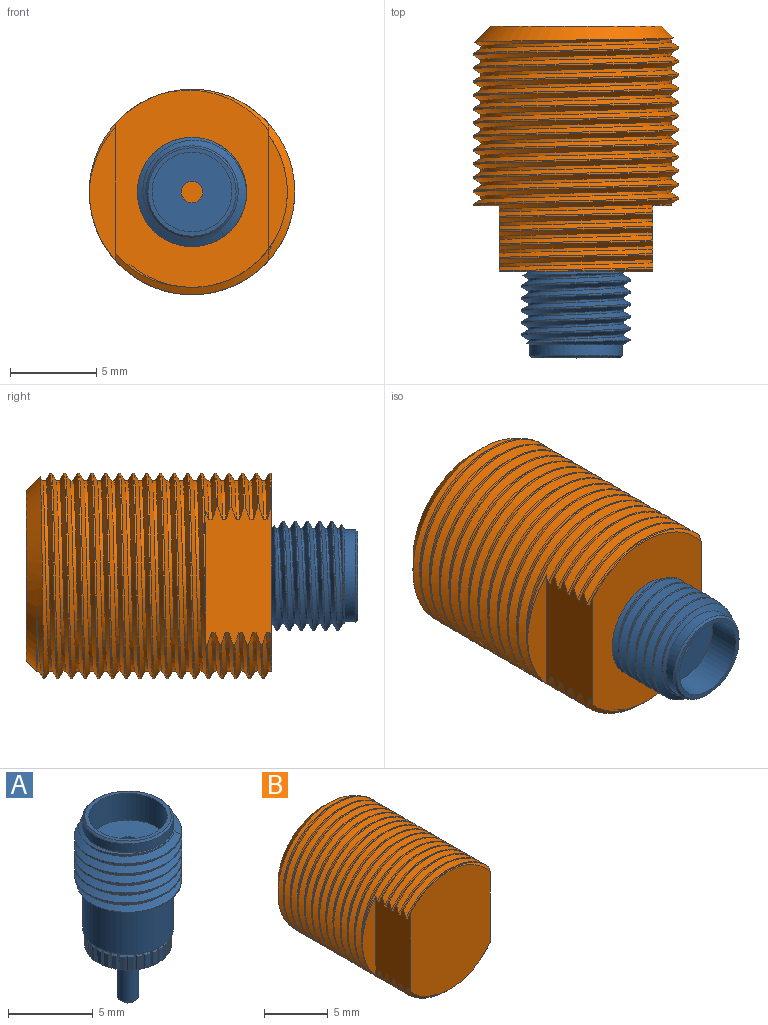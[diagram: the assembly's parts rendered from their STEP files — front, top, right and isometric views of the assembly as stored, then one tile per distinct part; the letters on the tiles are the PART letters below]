
ASSEMBLY  parts=2 mates=1
PART A: 177 faces, bbox 7.3x6.4x13.2 mm
  f0: cone r=0.38mm half-angle=45deg, axis (0,0,1), area 1.1mm2, adj f1,f176
  f1: cylinder r=0.64mm len=4.85mm, axis (0,0,1), area 19.4mm2, adj f0,f15
  f2: cylinder r=0.62mm len=6.2mm, axis (0,0,1), area 24.3mm2, adj f109,f175
  f3: cylinder r=2.74mm len=5.49mm, axis (0,0,-1), area 13.6mm2, adj f11,f12,f172,f173
  f4: cone r=2.67mm half-angle=45deg, axis (0,0,-1), area 2.8mm2, adj f6,f108
  f5: cylinder r=2.31mm len=4.63mm, axis (0,0,-1), area 28.1mm2, adj f108,f109
  f6: cylinder r=2.67mm len=5.35mm, axis (0,0,-1), area 10.8mm2, adj f4,f11
  f7: cylinder r=2.67mm len=5.35mm, axis (0,0,-1), area 52.1mm2, adj f12,f16
  f8: cylinder r=2.45mm len=4.9mm, axis (0,0,-1), area 3.1mm2, adj f9,f16,f76,f77,f78,f79,f80,f81
  f9: cone r=2.55mm half-angle=45deg, axis (0,0,-1), area 0.1mm2, adj f8,f10,f137,f138
  f10: cylinder r=2.55mm len=0.9mm, axis (0,0,-1), area 0.3mm2, adj f9,f34,f137,f138
  f11: cone r=3.16mm half-angle=60deg, axis (0,0,-1), area 5.5mm2, adj f3,f6,f13,f172,f173
  f12: cone r=2.67mm half-angle=60deg, axis (0,0,1), area 5.5mm2, adj f3,f7,f13,f172,f173
  f13: cylinder r=3.16mm len=6.33mm, axis (0,0,-1), area 9.1mm2, adj f11,f12,f172,f173
  f14: cylinder r=1.45mm len=2.9mm, axis (0,0,-1), area 11.6mm2, adj f15,f174
  f15: plane 2.9x2.9mm, normal (0,0,-1), area 5.3mm2, adj f1,f14
  f16: plane 5.35x5.35mm, normal (0,0,-1), area 3.6mm2, adj f7,f8
  f17: cone r=2.45mm half-angle=45deg, axis (0,0,1), area 0.1mm2, adj f47,f169,f170,f174
  f18: cone r=2.45mm half-angle=45deg, axis (0,0,1), area 0.1mm2, adj f48,f110,f171,f174
  f19: cone r=2.45mm half-angle=45deg, axis (0,0,1), area 0.1mm2, adj f49,f167,f168,f174
  f20: cone r=2.45mm half-angle=45deg, axis (0,0,1), area 0.1mm2, adj f50,f165,f166,f174
  f21: cone r=2.45mm half-angle=45deg, axis (0,0,1), area 0.1mm2, adj f51,f163,f164,f174
  f22: cone r=2.45mm half-angle=45deg, axis (0,0,1), area 0.1mm2, adj f52,f161,f162,f174
  f23: cone r=2.45mm half-angle=45deg, axis (0,0,1), area 0.1mm2, adj f53,f159,f160,f174
  f24: cone r=2.45mm half-angle=45deg, axis (0,0,1), area 0.1mm2, adj f54,f157,f158,f174
  f25: cone r=2.45mm half-angle=45deg, axis (0,0,1), area 0.1mm2, adj f55,f155,f156,f174
  f26: cone r=2.45mm half-angle=45deg, axis (0,0,1), area 0.1mm2, adj f56,f153,f154,f174
  f27: cone r=2.45mm half-angle=45deg, axis (0,0,1), area 0.1mm2, adj f57,f151,f152,f174
  f28: cone r=2.45mm half-angle=45deg, axis (0,0,1), area 0.1mm2, adj f58,f149,f150,f174
  f29: cone r=2.45mm half-angle=45deg, axis (0,0,1), area 0.1mm2, adj f59,f147,f148,f174
  f30: cone r=2.45mm half-angle=45deg, axis (0,0,1), area 0.1mm2, adj f60,f145,f146,f174
  f31: cone r=2.45mm half-angle=45deg, axis (0,0,1), area 0.1mm2, adj f61,f143,f144,f174
  f32: cone r=2.45mm half-angle=45deg, axis (0,0,1), area 0.1mm2, adj f62,f141,f142,f174
  f33: cone r=2.45mm half-angle=45deg, axis (0,0,1), area 0.1mm2, adj f63,f139,f140,f174
  f34: cone r=2.45mm half-angle=45deg, axis (0,0,1), area 0.1mm2, adj f10,f137,f138,f174
  f35: cone r=2.45mm half-angle=45deg, axis (0,0,1), area 0.1mm2, adj f64,f135,f136,f174
  f36: cone r=2.45mm half-angle=45deg, axis (0,0,1), area 0.1mm2, adj f65,f133,f134,f174
  f37: cone r=2.45mm half-angle=45deg, axis (0,0,1), area 0.1mm2, adj f66,f131,f132,f174
  f38: cone r=2.45mm half-angle=45deg, axis (0,0,1), area 0.1mm2, adj f67,f129,f130,f174
  f39: cone r=2.45mm half-angle=45deg, axis (0,0,1), area 0.1mm2, adj f68,f127,f128,f174
  f40: cone r=2.45mm half-angle=45deg, axis (0,0,1), area 0.1mm2, adj f69,f125,f126,f174
  f41: cone r=2.45mm half-angle=45deg, axis (0,0,1), area 0.1mm2, adj f70,f123,f124,f174
  f42: cone r=2.45mm half-angle=45deg, axis (0,0,1), area 0.1mm2, adj f71,f121,f122,f174
  f43: cone r=2.45mm half-angle=45deg, axis (0,0,1), area 0.1mm2, adj f72,f119,f120,f174
  f44: cone r=2.45mm half-angle=45deg, axis (0,0,1), area 0.1mm2, adj f73,f117,f118,f174
  f45: cone r=2.45mm half-angle=45deg, axis (0,0,1), area 0.1mm2, adj f74,f115,f116,f174
  f46: cone r=2.45mm half-angle=45deg, axis (0,0,1), area 0.1mm2, adj f75,f113,f114,f174
  f47: cylinder r=2.55mm len=0.9mm, axis (0,0,-1), area 0.3mm2, adj f17,f76,f169,f170
  f48: cylinder r=2.55mm len=0.9mm, axis (0,0,-1), area 0.3mm2, adj f18,f77,f110,f171
  f49: cylinder r=2.55mm len=0.9mm, axis (0,0,-1), area 0.3mm2, adj f19,f78,f167,f168
  f50: cylinder r=2.55mm len=0.9mm, axis (0,0,-1), area 0.3mm2, adj f20,f79,f165,f166
  f51: cylinder r=2.55mm len=0.9mm, axis (0,0,-1), area 0.3mm2, adj f21,f80,f163,f164
  f52: cylinder r=2.55mm len=0.9mm, axis (0,0,-1), area 0.3mm2, adj f22,f81,f161,f162
  f53: cylinder r=2.55mm len=0.9mm, axis (0,0,-1), area 0.3mm2, adj f23,f82,f159,f160
  f54: cylinder r=2.55mm len=0.9mm, axis (0,0,-1), area 0.3mm2, adj f24,f83,f157,f158
  f55: cylinder r=2.55mm len=0.9mm, axis (0,0,-1), area 0.3mm2, adj f25,f84,f155,f156
  f56: cylinder r=2.55mm len=0.9mm, axis (0,0,-1), area 0.3mm2, adj f26,f85,f153,f154
  f57: cylinder r=2.55mm len=0.9mm, axis (0,0,-1), area 0.3mm2, adj f27,f86,f151,f152
  f58: cylinder r=2.55mm len=0.9mm, axis (0,0,-1), area 0.3mm2, adj f28,f87,f149,f150
  f59: cylinder r=2.55mm len=0.9mm, axis (0,0,-1), area 0.3mm2, adj f29,f88,f147,f148
  f60: cylinder r=2.55mm len=0.9mm, axis (0,0,-1), area 0.3mm2, adj f30,f89,f145,f146
  f61: cylinder r=2.55mm len=0.9mm, axis (0,0,-1), area 0.3mm2, adj f31,f90,f143,f144
  f62: cylinder r=2.55mm len=0.9mm, axis (0,0,-1), area 0.3mm2, adj f32,f91,f141,f142
  f63: cylinder r=2.55mm len=0.9mm, axis (0,0,-1), area 0.3mm2, adj f33,f92,f139,f140
  f64: cylinder r=2.55mm len=0.9mm, axis (0,0,-1), area 0.3mm2, adj f35,f93,f135,f136
  f65: cylinder r=2.55mm len=0.9mm, axis (0,0,-1), area 0.3mm2, adj f36,f94,f133,f134
  f66: cylinder r=2.55mm len=0.9mm, axis (0,0,-1), area 0.3mm2, adj f37,f95,f131,f132
  f67: cylinder r=2.55mm len=0.9mm, axis (0,0,-1), area 0.3mm2, adj f38,f96,f129,f130
  f68: cylinder r=2.55mm len=0.9mm, axis (0,0,-1), area 0.3mm2, adj f39,f97,f127,f128
  f69: cylinder r=2.55mm len=0.9mm, axis (0,0,-1), area 0.3mm2, adj f40,f98,f125,f126
  f70: cylinder r=2.55mm len=0.9mm, axis (0,0,-1), area 0.3mm2, adj f41,f99,f123,f124
  f71: cylinder r=2.55mm len=0.9mm, axis (0,0,-1), area 0.3mm2, adj f42,f100,f121,f122
  f72: cylinder r=2.55mm len=0.9mm, axis (0,0,-1), area 0.3mm2, adj f43,f101,f119,f120
  f73: cylinder r=2.55mm len=0.9mm, axis (0,0,-1), area 0.3mm2, adj f44,f102,f117,f118
  f74: cylinder r=2.55mm len=0.9mm, axis (0,0,-1), area 0.3mm2, adj f45,f103,f115,f116
  f75: cylinder r=2.55mm len=0.9mm, axis (0,0,-1), area 0.3mm2, adj f46,f104,f113,f114
  f76: cone r=2.55mm half-angle=45deg, axis (0,0,-1), area 0.1mm2, adj f8,f47,f169,f170
  f77: cone r=2.55mm half-angle=45deg, axis (0,0,-1), area 0.1mm2, adj f8,f48,f110,f171
  f78: cone r=2.55mm half-angle=45deg, axis (0,0,-1), area 0.1mm2, adj f8,f49,f167,f168
  f79: cone r=2.55mm half-angle=45deg, axis (0,0,-1), area 0.1mm2, adj f8,f50,f165,f166
  f80: cone r=2.55mm half-angle=45deg, axis (0,0,-1), area 0.1mm2, adj f8,f51,f163,f164
  f81: cone r=2.55mm half-angle=45deg, axis (0,0,-1), area 0.1mm2, adj f8,f52,f161,f162
  f82: cone r=2.55mm half-angle=45deg, axis (0,0,-1), area 0.1mm2, adj f8,f53,f159,f160
  f83: cone r=2.55mm half-angle=45deg, axis (0,0,-1), area 0.1mm2, adj f8,f54,f157,f158
  f84: cone r=2.55mm half-angle=45deg, axis (0,0,-1), area 0.1mm2, adj f8,f55,f155,f156
  f85: cone r=2.55mm half-angle=45deg, axis (0,0,-1), area 0.1mm2, adj f8,f56,f153,f154
  f86: cone r=2.55mm half-angle=45deg, axis (0,0,-1), area 0.1mm2, adj f8,f57,f151,f152
  f87: cone r=2.55mm half-angle=45deg, axis (0,0,-1), area 0.1mm2, adj f8,f58,f149,f150
  f88: cone r=2.55mm half-angle=45deg, axis (0,0,-1), area 0.1mm2, adj f8,f59,f147,f148
  f89: cone r=2.55mm half-angle=45deg, axis (0,0,-1), area 0.1mm2, adj f8,f60,f145,f146
  f90: cone r=2.55mm half-angle=45deg, axis (0,0,-1), area 0.1mm2, adj f8,f61,f143,f144
  f91: cone r=2.55mm half-angle=45deg, axis (0,0,-1), area 0.1mm2, adj f8,f62,f141,f142
  f92: cone r=2.55mm half-angle=45deg, axis (0,0,-1), area 0.1mm2, adj f8,f63,f139,f140
  f93: cone r=2.55mm half-angle=45deg, axis (0,0,-1), area 0.1mm2, adj f8,f64,f135,f136
  f94: cone r=2.55mm half-angle=45deg, axis (0,0,-1), area 0.1mm2, adj f8,f65,f133,f134
  f95: cone r=2.55mm half-angle=45deg, axis (0,0,-1), area 0.1mm2, adj f8,f66,f131,f132
  f96: cone r=2.55mm half-angle=45deg, axis (0,0,-1), area 0.1mm2, adj f8,f67,f129,f130
  f97: cone r=2.55mm half-angle=45deg, axis (0,0,-1), area 0.1mm2, adj f8,f68,f127,f128
  f98: cone r=2.55mm half-angle=45deg, axis (0,0,-1), area 0.1mm2, adj f8,f69,f125,f126
  f99: cone r=2.55mm half-angle=45deg, axis (0,0,-1), area 0.1mm2, adj f8,f70,f123,f124
  f100: cone r=2.55mm half-angle=45deg, axis (0,0,-1), area 0.1mm2, adj f8,f71,f121,f122
  f101: cone r=2.55mm half-angle=45deg, axis (0,0,-1), area 0.1mm2, adj f8,f72,f119,f120
  f102: cone r=2.55mm half-angle=45deg, axis (0,0,-1), area 0.1mm2, adj f8,f73,f117,f118
  f103: cone r=2.55mm half-angle=45deg, axis (0,0,-1), area 0.1mm2, adj f8,f74,f115,f116
  f104: cone r=2.55mm half-angle=45deg, axis (0,0,-1), area 0.1mm2, adj f8,f75,f113,f114
  f105: cone r=2.45mm half-angle=45deg, axis (0,0,1), area 0.1mm2, adj f106,f111,f112,f174
  f106: cylinder r=2.55mm len=0.9mm, axis (0,0,-1), area 0.3mm2, adj f105,f107,f111,f112
  f107: cone r=2.55mm half-angle=45deg, axis (0,0,-1), area 0.1mm2, adj f8,f106,f111,f112
  f108: plane 5.11x5.11mm, normal (0,0,1), area 3.7mm2, adj f4,f5
  f109: plane 4.63x4.63mm, normal (0,0,1), area 15.6mm2, adj f2,f5
  f110: plane 1.1x0.13mm, normal (0.93,-0.37,0), area 0.1mm2, adj f18,f48,f77,f111
  f111: plane 1.1x0.13mm, normal (-0.37,-0.93,0), area 0.1mm2, adj f105,f106,f107,f110
  f112: plane 1.1x0.14mm, normal (0.98,-0.18,0), area 0.1mm2, adj f105,f106,f107,f113
  f113: plane 1.1x0.14mm, normal (-0.18,-0.98,0), area 0.1mm2, adj f46,f75,f104,f112
  f114: plane 1.1x0.14mm, normal (1,0.03,0), area 0.1mm2, adj f46,f75,f104,f115
  f115: plane 1.1x0.14mm, normal (0.03,-1,0), area 0.1mm2, adj f45,f74,f103,f114
  f116: plane 1.1x0.14mm, normal (0.97,0.23,0), area 0.1mm2, adj f45,f74,f103,f117
  f117: plane 1.1x0.14mm, normal (0.23,-0.97,0), area 0.1mm2, adj f44,f73,f102,f116
  f118: plane 1.1x0.13mm, normal (0.91,0.42,0), area 0.1mm2, adj f44,f73,f102,f119
  f119: plane 1.1x0.13mm, normal (0.42,-0.91,0), area 0.1mm2, adj f43,f72,f101,f118
  f120: plane 1.1x0.11mm, normal (0.81,0.59,0), area 0.1mm2, adj f43,f72,f101,f121
  f121: plane 1.1x0.11mm, normal (0.59,-0.81,0), area 0.1mm2, adj f42,f71,f100,f120
  f122: plane 1.1x0.11mm, normal (0.67,0.74,0), area 0.1mm2, adj f42,f71,f100,f123
  f123: plane 1.1x0.11mm, normal (0.74,-0.67,0), area 0.1mm2, adj f41,f70,f99,f122
  f124: plane 1.1x0.12mm, normal (0.51,0.86,0), area 0.1mm2, adj f41,f70,f99,f125
  f125: plane 1.1x0.12mm, normal (0.86,-0.51,0), area 0.1mm2, adj f40,f69,f98,f124
  f126: plane 1.1x0.13mm, normal (0.32,0.95,0), area 0.1mm2, adj f40,f69,f98,f127
  f127: plane 1.1x0.13mm, normal (0.95,-0.32,0), area 0.1mm2, adj f39,f68,f97,f126
  f128: plane 1.1x0.14mm, normal (0.13,0.99,0), area 0.1mm2, adj f39,f68,f97,f129
  f129: plane 1.1x0.14mm, normal (0.99,-0.13,0), area 0.1mm2, adj f38,f67,f96,f128
  f130: plane 1.1x0.14mm, normal (-0.08,1,0), area 0.1mm2, adj f38,f67,f96,f131
  f131: plane 1.1x0.14mm, normal (1,0.08,0), area 0.1mm2, adj f37,f66,f95,f130
  f132: plane 1.1x0.14mm, normal (-0.28,0.96,0), area 0.1mm2, adj f37,f66,f95,f133
  f133: plane 1.1x0.14mm, normal (0.96,0.28,0), area 0.1mm2, adj f36,f65,f94,f132
  f134: plane 1.1x0.13mm, normal (-0.46,0.89,0), area 0.1mm2, adj f36,f65,f94,f135
  f135: plane 1.1x0.13mm, normal (0.89,0.46,0), area 0.1mm2, adj f35,f64,f93,f134
  f136: plane 1.1x0.11mm, normal (-0.63,0.78,0), area 0.1mm2, adj f35,f64,f93,f137
  f137: plane 1.1x0.11mm, normal (0.78,0.63,0), area 0.1mm2, adj f9,f10,f34,f136
  f138: plane 1.1x0.11mm, normal (-0.78,0.63,0), area 0.1mm2, adj f9,f10,f34,f139
  f139: plane 1.1x0.11mm, normal (0.63,0.78,0), area 0.1mm2, adj f33,f63,f92,f138
  f140: plane 1.1x0.13mm, normal (-0.89,0.46,0), area 0.1mm2, adj f33,f63,f92,f141
  f141: plane 1.1x0.13mm, normal (0.46,0.89,0), area 0.1mm2, adj f32,f62,f91,f140
  f142: plane 1.1x0.14mm, normal (-0.96,0.28,0), area 0.1mm2, adj f32,f62,f91,f143
  f143: plane 1.1x0.14mm, normal (0.28,0.96,0), area 0.1mm2, adj f31,f61,f90,f142
  f144: plane 1.1x0.14mm, normal (-1,0.08,0), area 0.1mm2, adj f31,f61,f90,f145
  f145: plane 1.1x0.14mm, normal (0.08,1,0), area 0.1mm2, adj f30,f60,f89,f144
  f146: plane 1.1x0.14mm, normal (-0.99,-0.13,0), area 0.1mm2, adj f30,f60,f89,f147
  f147: plane 1.1x0.14mm, normal (-0.13,0.99,0), area 0.1mm2, adj f29,f59,f88,f146
  f148: plane 1.1x0.13mm, normal (-0.95,-0.32,0), area 0.1mm2, adj f29,f59,f88,f149
  f149: plane 1.1x0.13mm, normal (-0.32,0.95,0), area 0.1mm2, adj f28,f58,f87,f148
  f150: plane 1.1x0.12mm, normal (-0.86,-0.51,0), area 0.1mm2, adj f28,f58,f87,f151
  f151: plane 1.1x0.12mm, normal (-0.51,0.86,0), area 0.1mm2, adj f27,f57,f86,f150
  f152: plane 1.1x0.11mm, normal (-0.74,-0.67,0), area 0.1mm2, adj f27,f57,f86,f153
  f153: plane 1.1x0.11mm, normal (-0.67,0.74,0), area 0.1mm2, adj f26,f56,f85,f152
  f154: plane 1.1x0.11mm, normal (-0.59,-0.81,0), area 0.1mm2, adj f26,f56,f85,f155
  f155: plane 1.1x0.11mm, normal (-0.81,0.59,0), area 0.1mm2, adj f25,f55,f84,f154
  f156: plane 1.1x0.13mm, normal (-0.42,-0.91,0), area 0.1mm2, adj f25,f55,f84,f157
  f157: plane 1.1x0.13mm, normal (-0.91,0.42,0), area 0.1mm2, adj f24,f54,f83,f156
  f158: plane 1.1x0.14mm, normal (-0.23,-0.97,0), area 0.1mm2, adj f24,f54,f83,f159
  f159: plane 1.1x0.14mm, normal (-0.97,0.23,0), area 0.1mm2, adj f23,f53,f82,f158
  f160: plane 1.1x0.14mm, normal (-0.03,-1,0), area 0.1mm2, adj f23,f53,f82,f161
  f161: plane 1.1x0.14mm, normal (-1,0.03,0), area 0.1mm2, adj f22,f52,f81,f160
  f162: plane 1.1x0.14mm, normal (0.18,-0.98,0), area 0.1mm2, adj f22,f52,f81,f163
  f163: plane 1.1x0.14mm, normal (-0.98,-0.18,0), area 0.1mm2, adj f21,f51,f80,f162
  f164: plane 1.1x0.13mm, normal (0.37,-0.93,0), area 0.1mm2, adj f21,f51,f80,f165
  f165: plane 1.1x0.13mm, normal (-0.93,-0.37,0), area 0.1mm2, adj f20,f50,f79,f164
  f166: plane 1.1x0.12mm, normal (0.55,-0.83,0), area 0.1mm2, adj f20,f50,f79,f167
  f167: plane 1.1x0.12mm, normal (-0.83,-0.55,0), area 0.1mm2, adj f19,f49,f78,f166
  f168: plane 1.1x0.1mm, normal (0.71,-0.71,0), area 0.1mm2, adj f19,f49,f78,f169
  f169: plane 1.1x0.1mm, normal (-0.71,-0.71,0), area 0.1mm2, adj f17,f47,f76,f168
  f170: plane 1.1x0.12mm, normal (0.83,-0.55,0), area 0.1mm2, adj f17,f47,f76,f171
  f171: plane 1.1x0.12mm, normal (-0.55,-0.83,0), area 0.1mm2, adj f18,f48,f77,f170
  f172: bspline ~7.33x6.35mm, area 49.8mm2, adj f3,f11,f12,f13
  f173: bspline ~7.33x6.35mm, area 49.8mm2, adj f3,f11,f12,f13
  f174: plane 4.9x4.9mm, normal (0,0,-1), area 12.3mm2, adj f14,f17,f18,f19,f20,f21,f22,f23
  f175: plane 1.25x1.25mm, normal (0,0,1), area 1.2mm2, adj f2
  f176: plane 0.77x0.77mm, normal (0,0,-1), area 0.5mm2, adj f0
PART B: 49 faces, bbox 12x14.6x12 mm
  f0: cylinder r=5.95mm len=11.91mm, axis (0,1,0), area 44.9mm2, adj f1,f11,f41,f42,f44,f45,f47
  f1: cone r=5.95mm half-angle=45deg, axis (0,-1,0), area 36.8mm2, adj f0,f40,f41,f42,f43
  f2: cylinder r=5.95mm len=8.89mm, axis (0,1,0), area 1mm2, adj f12,f21,f45,f47
  f3: cylinder r=5.95mm len=8.89mm, axis (0,1,0), area 1mm2, adj f13,f22,f45,f47
  f4: cylinder r=5.95mm len=8.89mm, axis (0,1,0), area 1mm2, adj f14,f23,f45,f47
  f5: cylinder r=5.95mm len=8.89mm, axis (0,1,0), area 1mm2, adj f15,f24,f45,f47
  f6: cylinder r=5.95mm len=8.89mm, axis (0,1,0), area 1mm2, adj f16,f30,f45,f47
  f7: cylinder r=5.95mm len=8.89mm, axis (0,1,0), area 1mm2, adj f17,f26,f45,f47
  f8: cylinder r=5.95mm len=8.89mm, axis (0,1,0), area 1mm2, adj f18,f27,f45,f47
  f9: cylinder r=5.95mm len=8.89mm, axis (0,1,0), area 1mm2, adj f19,f28,f45,f47
  f10: cylinder r=5.95mm len=8.89mm, axis (0,1,0), area 0.9mm2, adj f20,f25,f45,f46,f47
  f11: bspline ~11.91x5.95mm, area 5.1mm2, adj f0,f31,f45,f47
  f12: bspline ~11.91x5.95mm, area 5.1mm2, adj f2,f32,f45,f47
  f13: bspline ~11.91x5.95mm, area 5.1mm2, adj f3,f33,f45,f47
  f14: bspline ~11.91x5.95mm, area 5.1mm2, adj f4,f34,f45,f47
  f15: bspline ~11.91x5.95mm, area 5.1mm2, adj f5,f35,f45,f47
  f16: bspline ~11.91x5.95mm, area 5.1mm2, adj f6,f36,f45,f47
  f17: bspline ~11.91x5.95mm, area 5.1mm2, adj f7,f37,f45,f47
  f18: bspline ~11.91x5.95mm, area 5.1mm2, adj f8,f38,f45,f47
  f19: bspline ~11.91x5.95mm, area 5.1mm2, adj f9,f39,f45,f47
  f20: bspline ~6.32x2.39mm, area 1mm2, adj f10,f46,f47
  f21: bspline ~11.91x5.95mm, area 5.1mm2, adj f2,f31,f45,f47
  f22: bspline ~11.91x5.95mm, area 5.1mm2, adj f3,f32,f45,f47
  f23: bspline ~11.91x5.95mm, area 5.1mm2, adj f4,f33,f45,f47
  f24: bspline ~11.91x5.95mm, area 5.1mm2, adj f5,f34,f45,f47
  f25: bspline ~11.91x5.95mm, area 5.1mm2, adj f10,f39,f45,f47
  f26: bspline ~11.91x5.95mm, area 5.1mm2, adj f7,f36,f45,f47
  f27: bspline ~11.91x5.95mm, area 5.1mm2, adj f8,f37,f45,f47
  f28: bspline ~11.91x5.95mm, area 5.1mm2, adj f9,f38,f45,f47
  f29: bspline ~5.95x5.95mm, area 0.5mm2, adj f35,f45,f46
  f30: bspline ~11.91x5.95mm, area 5.1mm2, adj f6,f43,f45,f47
  f31: bspline ~11.05x5.52mm, area 2.1mm2, adj f11,f21,f45,f47
  f32: bspline ~11.05x5.52mm, area 2.1mm2, adj f12,f22,f45,f47
  f33: bspline ~11.05x5.52mm, area 2.1mm2, adj f13,f23,f45,f47
  f34: bspline ~11.05x5.52mm, area 2.1mm2, adj f14,f24,f45,f47
  f35: bspline ~11.05x5.52mm, area 1.7mm2, adj f15,f29,f45,f46,f47
  f36: bspline ~11.05x5.52mm, area 2.1mm2, adj f16,f26,f45,f47
  f37: bspline ~11.05x5.52mm, area 2.1mm2, adj f17,f27,f45,f47
  f38: bspline ~11.05x5.52mm, area 2.1mm2, adj f18,f28,f45,f47
  f39: bspline ~11.05x5.52mm, area 2.1mm2, adj f19,f25,f45,f47
  f40: plane 9.87x9.87mm, normal (0,1,0), area 76.6mm2, adj f1
  f41: bspline ~11.91x11.91mm, area 217.8mm2, adj f0,f1,f43,f44,f45
  f42: bspline ~11.91x11.91mm, area 219mm2, adj f0,f1,f43,f47,f48
  f43: bspline ~11.05x11.02mm, area 87.2mm2, adj f1,f30,f41,f42,f45,f47,f48
  f44: plane 7.73x1.54mm, normal (0,-1,0), area 7.9mm2, adj f0,f41,f45
  f45: plane 7.94x3.83mm, normal (-1,0,0), area 27.2mm2, adj f0,f2,f3,f4,f5,f6,f7,f8
  f46: plane 11.56x9mm, normal (0,-1,0), area 90.1mm2, adj f10,f20,f29,f35,f45,f47
  f47: plane 7.94x3.83mm, normal (1,0,0), area 27.4mm2, adj f0,f2,f3,f4,f5,f6,f7,f8
  f48: plane 6.67x1.13mm, normal (0,-1,0), area 4.8mm2, adj f42,f43,f47
PLACE A rot(axis=(1,0,0),90deg) t=(-7.65,-16.74,2.42)mm
PLACE B t=(-7.65,-9.11,8.78)mm
MATE fastened A.f0 <-> B.f0  axis (0,1,0) through (-7.65,-23.34,8.78)mm
